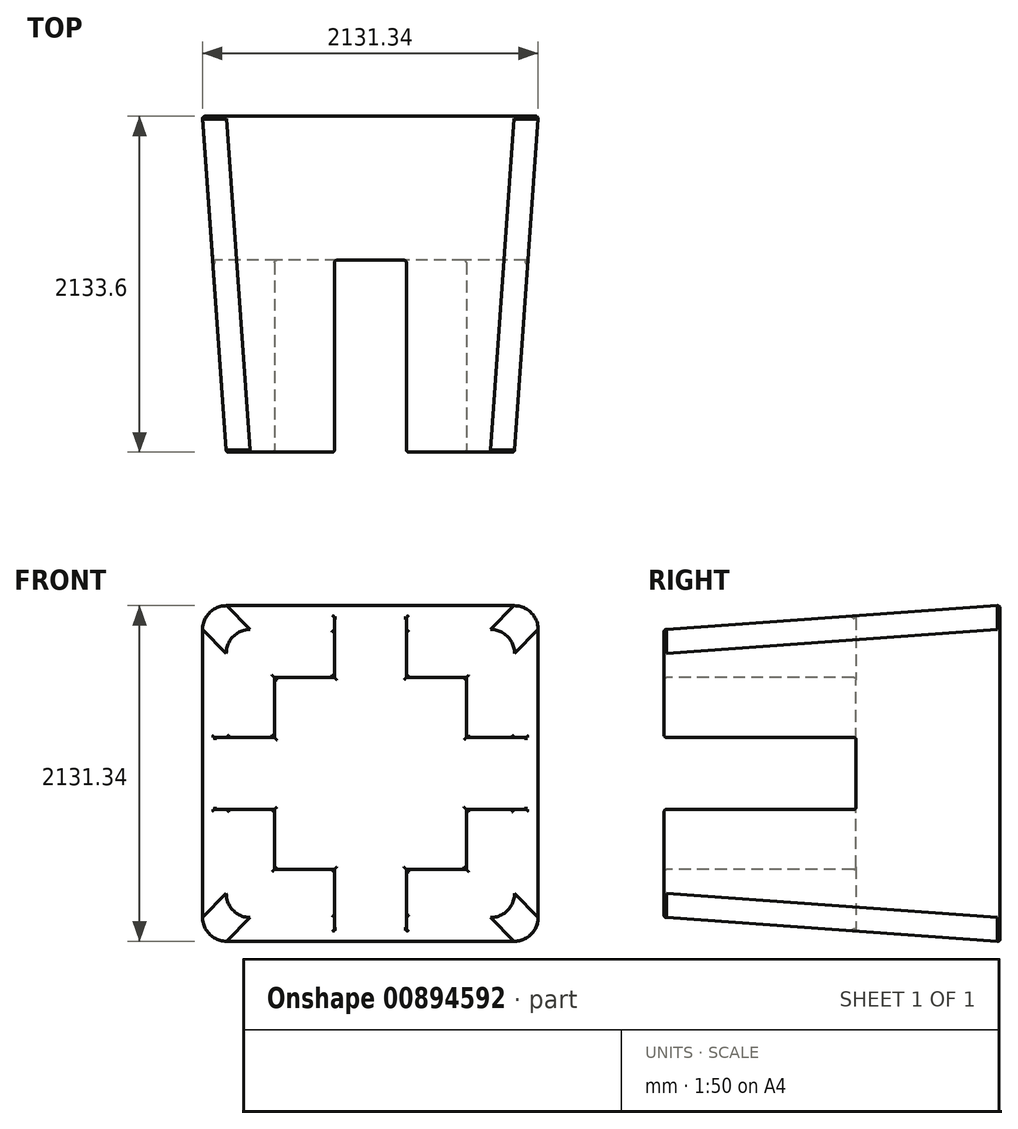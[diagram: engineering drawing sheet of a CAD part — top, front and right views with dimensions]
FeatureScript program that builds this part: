
annotation { "Feature Type Name" : "Feature", "Feature Type Description" : "" }
export const myFeature = defineFeature(function(context is Context, id is Id, definition is map)
    precondition{}
    {
        {
            var Q0;
            Q0=qCreatedBy(makeId("Front.planeOp"),FACE);
            var sketch = newSketch(context, id + "F0", { "sketchPlane" : qUnion([Q0])});
            skLineSegment(sketch, "E0.bottom", {"start": v(-914.4, 1066.8) * mm, "end": v(914.4, 1066.8) * mm});
            skLineSegment(sketch, "E0.top", {"start": v(-914.4, -1066.8) * mm, "end": v(914.4, -1066.8) * mm});
            skLineSegment(sketch, "E0.left", {"start": v(-1066.8, 914.4) * mm, "end": v(-1066.8, -914.4) * mm});
            skLineSegment(sketch, "E0.right", {"start": v(1066.8, 914.4) * mm, "end": v(1066.8, -914.4) * mm});
            skPoint(sketch, "E1.visualSharp", {"position": v(-1066.8, 1066.8) * mm});
            skArc(sketch, "E1.filletArc", {"start": v(-914.4, 1066.8) * mm, "mid": v(-1022.16, 1022.16) * mm, "end": v(-1066.8, 914.4) * mm});
            skPoint(sketch, "E2.visualSharp", {"position": v(1066.8, 1066.8) * mm});
            skArc(sketch, "E2.filletArc", {"start": v(1066.8, 914.4) * mm, "mid": v(1022.16, 1022.16) * mm, "end": v(914.4, 1066.8) * mm});
            skPoint(sketch, "E3.visualSharp", {"position": v(1066.8, -1066.8) * mm});
            skArc(sketch, "E3.filletArc", {"start": v(914.4, -1066.8) * mm, "mid": v(1022.16, -1022.16) * mm, "end": v(1066.8, -914.4) * mm});
            skPoint(sketch, "E4.visualSharp", {"position": v(-1066.8, -1066.8) * mm});
            skArc(sketch, "E4.filletArc", {"start": v(-1066.8, -914.4) * mm, "mid": v(-1022.16, -1022.16) * mm, "end": v(-914.4, -1066.8) * mm});
            skSolve(sketch);
        }
        {
            var Q0;
            Q0=qCreatedBy(makeId("Front.planeOp"),FACE);
            cPlane(context, id + "F1", {"entities" : qUnion([Q0]), "cplaneType" : CPlaneType.OFFSET, "offset" : 2133.6 * mm, "width" : 152.4 * mm, "height" : 152.4 * mm});
        }
        {
            var Q0;
            Q0=qCreatedBy(id+"F1.planeOp",FACE);
            var sketch = newSketch(context, id + "F2", { "sketchPlane" : qUnion([Q0])});
            skLineSegment(sketch, "E5.bottom", {"start": v(-762, 914.4) * mm, "end": v(762, 914.4) * mm});
            skLineSegment(sketch, "E5.top", {"start": v(-762, -914.4) * mm, "end": v(762, -914.4) * mm});
            skLineSegment(sketch, "E5.left", {"start": v(-914.4, 762) * mm, "end": v(-914.4, -762) * mm});
            skLineSegment(sketch, "E5.right", {"start": v(914.4, 762) * mm, "end": v(914.4, -762) * mm});
            skPoint(sketch, "E6.visualSharp", {"position": v(-914.4, 914.4) * mm});
            skArc(sketch, "E6.filletArc", {"start": v(-762, 914.4) * mm, "mid": v(-869.76, 869.76) * mm, "end": v(-914.4, 762) * mm});
            skPoint(sketch, "E7.visualSharp", {"position": v(914.4, 914.4) * mm});
            skArc(sketch, "E7.filletArc", {"start": v(914.4, 762) * mm, "mid": v(869.76, 869.76) * mm, "end": v(762, 914.4) * mm});
            skPoint(sketch, "E8.visualSharp", {"position": v(914.4, -914.4) * mm});
            skArc(sketch, "E8.filletArc", {"start": v(762, -914.4) * mm, "mid": v(869.76, -869.76) * mm, "end": v(914.4, -762) * mm});
            skPoint(sketch, "E9.visualSharp", {"position": v(-914.4, -914.4) * mm});
            skArc(sketch, "E9.filletArc", {"start": v(-914.4, -762) * mm, "mid": v(-869.76, -869.76) * mm, "end": v(-762, -914.4) * mm});
            skSolve(sketch);
        }
        {
            var Q0;
            Q0=makeQuery(id+"F2.imprint","IMPRINT",FACE,{"disambiguationData":[TD([[makeQuery(id+"F2.imprint","IMPRINT",EDGE,{"derivedFrom":sQuery(id+"F2.wireOp",EDGE,"E5.bottom")}),-1.0]])]});
            var Q1;
            Q1=makeQuery(id+"F0.imprint","IMPRINT",FACE,{"disambiguationData":[TD([[makeQuery(id+"F0.imprint","IMPRINT",EDGE,{"derivedFrom":sQuery(id+"F0.wireOp",EDGE,"E0.bottom")}),-1.0]])]});
            loft(context, id + "F3", {"sheetProfilesArray" : [{ "sheetProfileEntities" : qUnion([Q0]) }, { "sheetProfileEntities" : qUnion([Q1]) }]});
        }
        {
            var Q0;
            Q0=makeQuery(id+"F3.opLoft","CAP_FACE",FACE,{"disambiguationData":[OSD([makeQuery(id+"F2.imprint","IMPRINT",FACE,{"disambiguationData":[TD([[makeQuery(id+"F2.imprint","IMPRINT",EDGE,{"derivedFrom":sQuery(id+"F2.wireOp",EDGE,"E5.bottom")}),-1.0]])]})])],"isStart":true});
            var sketch = newSketch(context, id + "F4", { "sketchPlane" : qUnion([Q0])});
            skLineSegment(sketch, "E10.bottom", {"start": v(609.6, -609.6) * mm, "end": v(-609.6, -609.6) * mm});
            skLineSegment(sketch, "E10.top", {"start": v(609.6, 609.6) * mm, "end": v(-609.6, 609.6) * mm});
            skLineSegment(sketch, "E10.left", {"start": v(609.6, -609.6) * mm, "end": v(609.6, 609.6) * mm});
            skLineSegment(sketch, "E10.right", {"start": v(-609.6, -609.6) * mm, "end": v(-609.6, 609.6) * mm});
            skPoint(sketch, "E10.middle", {"position": v(0, 0) * mm});
            skSolve(sketch);
        }
        {
            var Q0;
            Q0 = qSketchRegion(id + "F4", true);
            extrude(context, id + "F5", {"entities" : qUnion([Q0]), "operationType" : NewBodyOperationType.REMOVE, "oppositeDirection" : true, "depth" : 1219.2 * mm, "offsetDistance" : 30.48 * mm});
        }
        {
            var Q0;
            Q0=makeQuery(id+"F3.opLoft","CAP_FACE",FACE,{"disambiguationData":[OSD([makeQuery(id+"F2.imprint","IMPRINT",FACE,{"disambiguationData":[TD([[makeQuery(id+"F2.imprint","IMPRINT",EDGE,{"derivedFrom":sQuery(id+"F2.wireOp",EDGE,"E5.bottom")}),-1.0]])]})])],"isStart":true});
            var sketch = newSketch(context, id + "F6", { "sketchPlane" : qUnion([Q0])});
            skLineSegment(sketch, "E11.bottom", {"start": v(1066.8, -228.6) * mm, "end": v(228.6, -228.6) * mm});
            skLineSegment(sketch, "E11.top", {"start": v(1066.8, 228.6) * mm, "end": v(228.6, 228.6) * mm});
            skLineSegment(sketch, "E11.left", {"start": v(1066.8, -228.6) * mm, "end": v(1066.8, 228.6) * mm});
            skLineSegment(sketch, "E11.right", {"start": v(-1066.8, -228.6) * mm, "end": v(-1066.8, 228.6) * mm});
            skPoint(sketch, "E11.middle", {"position": v(0, 0) * mm});
            skLineSegment(sketch, "E12.bottom", {"start": v(228.6, 1066.8) * mm, "end": v(-228.6, 1066.8) * mm});
            skLineSegment(sketch, "E12.top", {"start": v(228.6, -1066.8) * mm, "end": v(-228.6, -1066.8) * mm});
            skLineSegment(sketch, "E12.left", {"start": v(228.6, 1066.8) * mm, "end": v(228.6, 228.6) * mm});
            skLineSegment(sketch, "E12.right", {"start": v(-228.6, 1066.8) * mm, "end": v(-228.6, 228.6) * mm});
            skLineSegment(sketch, "E13.trimOffspring", {"start": v(-228.6, 228.6) * mm, "end": v(-1066.8, 228.6) * mm});
            skLineSegment(sketch, "E14.trimOffspring", {"start": v(-228.6, -228.6) * mm, "end": v(-228.6, -1066.8) * mm});
            skLineSegment(sketch, "E15.trimOffspring", {"start": v(-228.6, -228.6) * mm, "end": v(-1066.8, -228.6) * mm});
            skLineSegment(sketch, "E16.trimOffspring", {"start": v(228.6, -228.6) * mm, "end": v(228.6, -1066.8) * mm});
            skSolve(sketch);
        }
        {
            var Q0;
            Q0 = qSketchRegion(id + "F6", true);
            extrude(context, id + "F7", {"entities" : qUnion([Q0]), "operationType" : NewBodyOperationType.REMOVE, "oppositeDirection" : true, "depth" : 1219.2 * mm, "offsetDistance" : 30.48 * mm});
        }
        {
            var Q0;
            Q0=makeQuery(id+"F7.boolean.opBoolean","SPLIT",FACE,{"disambiguationData":[TD([makeQuery(id+"F7.opExtrude","SWEPT_FACE",FACE,{"disambiguationData":[OSD([sQuery(id+"F6.wireOp",EDGE,"E11.bottom")])]})])],"derivedFrom":makeQuery(id+"F3.opLoft","CAP_FACE",FACE,{"disambiguationData":[OSD([makeQuery(id+"F2.imprint","IMPRINT",FACE,{"disambiguationData":[TD([[makeQuery(id+"F2.imprint","IMPRINT",EDGE,{"derivedFrom":sQuery(id+"F2.wireOp",EDGE,"E5.bottom")}),-1.0]])]})])],"isStart":true})});
            var Q1;
            {var subQ5=sQuery(id+"F2.wireOp",EDGE,"E5.bottom");Q1=makeQuery(id+"F7.boolean.opBoolean","SPLIT",FACE,{"disambiguationData":[TD([makeQuery(id+"F7.opExtrude","SWEPT_FACE",FACE,{"disambiguationData":[OSD([sQuery(id+"F6.wireOp",EDGE,"E11.top")])]})])],"derivedFrom":makeQuery(id+"F3.opLoft","CAP_FACE",FACE,{"disambiguationData":[OSD([makeQuery(id+"F2.imprint","IMPRINT",FACE,{"disambiguationData":[TD([[makeQuery(id+"F2.imprint","IMPRINT",EDGE,{"derivedFrom":subQ5}),-1.0]])]})])],"isStart":true})});}
            var Q2;
            {var subQ5=sQuery(id+"F2.wireOp",EDGE,"E5.bottom");Q2=makeQuery(id+"F7.boolean.opBoolean","SPLIT",FACE,{"disambiguationData":[TD([makeQuery(id+"F7.opExtrude","SWEPT_FACE",FACE,{"disambiguationData":[OSD([sQuery(id+"F6.wireOp",EDGE,"E12.right")])]})])],"derivedFrom":makeQuery(id+"F3.opLoft","CAP_FACE",FACE,{"disambiguationData":[OSD([makeQuery(id+"F2.imprint","IMPRINT",FACE,{"disambiguationData":[TD([[makeQuery(id+"F2.imprint","IMPRINT",EDGE,{"derivedFrom":subQ5}),-1.0]])]})])],"isStart":true})});}
            var Q3;
            Q3=makeQuery(id+"F7.boolean.opBoolean","SPLIT",FACE,{"disambiguationData":[TD([makeQuery(id+"F7.opExtrude","SWEPT_FACE",FACE,{"disambiguationData":[OSD([sQuery(id+"F6.wireOp",EDGE,"E14.trimOffspring")])]})])],"derivedFrom":makeQuery(id+"F3.opLoft","CAP_FACE",FACE,{"disambiguationData":[OSD([makeQuery(id+"F2.imprint","IMPRINT",FACE,{"disambiguationData":[TD([[makeQuery(id+"F2.imprint","IMPRINT",EDGE,{"derivedFrom":sQuery(id+"F2.wireOp",EDGE,"E5.bottom")}),-1.0]])]})])],"isStart":true})});
            var Q4;
            Q4=makeQuery(id+"F7.boolean.opBoolean","MERGE",FACE,{"derivedFrom":[makeQuery(id+"F5.boolean.opBoolean","COPY",FACE,{"derivedFrom":makeQuery(id+"F5.opExtrude","CAP_FACE",FACE,{"disambiguationData":[OSD([sQuery(id+"F4.wireOp",EDGE,"E10.bottom"),sQuery(id+"F4.wireOp",EDGE,"E10.top"),sQuery(id+"F4.wireOp",EDGE,"E10.left"),sQuery(id+"F4.wireOp",EDGE,"E10.right")])],"isStart":false})})],"fromTools":[makeQuery(id+"F7.opExtrude","CAP_FACE",FACE,{"disambiguationData":[OSD([sQuery(id+"F6.wireOp",EDGE,"E11.bottom"),sQuery(id+"F6.wireOp",EDGE,"E11.top"),sQuery(id+"F6.wireOp",EDGE,"E11.left"),sQuery(id+"F6.wireOp",EDGE,"E11.right"),sQuery(id+"F6.wireOp",EDGE,"E12.bottom"),sQuery(id+"F6.wireOp",EDGE,"E12.top"),sQuery(id+"F6.wireOp",EDGE,"E12.left"),sQuery(id+"F6.wireOp",EDGE,"E12.right"),sQuery(id+"F6.wireOp",EDGE,"E13.trimOffspring"),sQuery(id+"F6.wireOp",EDGE,"E14.trimOffspring"),sQuery(id+"F6.wireOp",EDGE,"E15.trimOffspring"),sQuery(id+"F6.wireOp",EDGE,"E16.trimOffspring")])],"isStart":false})]});
            var Q5;
            Q5=makeQuery(id+"F3.opLoft","CAP_FACE",FACE,{"disambiguationData":[OSD([makeQuery(id+"F0.imprint","IMPRINT",FACE,{"disambiguationData":[TD([[makeQuery(id+"F0.imprint","IMPRINT",EDGE,{"derivedFrom":sQuery(id+"F0.wireOp",EDGE,"E0.bottom")}),-1.0]])]})])],"isStart":true});
            fillet(context, id + "F8", {"entities" : qUnion([Q0, Q1, Q2, Q3, Q4, Q5]), "radius" : 15.24 * mm, "tangentPropagation" : true, "allowEdgeOverflow" : false});
        }
    });
